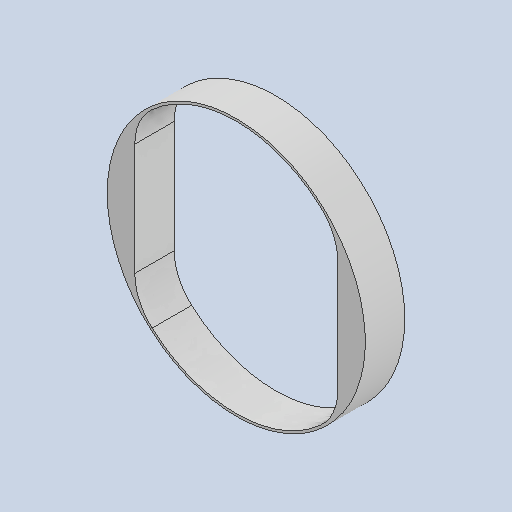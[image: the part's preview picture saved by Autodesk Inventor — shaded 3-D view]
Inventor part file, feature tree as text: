
AUTODESK INVENTOR PART (.ipt)
format: ipt  version: 2022 (Build 260153000, 153)  size: 126,976 bytes
history: native  units: in
note: dims shown in document units (in); Inventor stores cm internally (conversion verified against a paired STEP export)
features: other x3, sketch x1, plane x1, extrude x1, reference x1
ambient origin geometry x8: Origin, YZ Plane, XZ Plane, XY Plane, X Axis, Y Axis, Z Axis, Center Point
bodies: Solid1 (feature_tree)
feature tree (7):
  sketch  "Sketch1"  dims[d2=0.375in d3=0.0in d20=0.0157in d21=0.0394in]
  plane  "Work Plane1"
  extrude  "Extrusion1"  Depth=0.0157in
  reference  "Reference1"
  other  "<userpath>\Documents\CAD\guardSwerve1\Assembly1.iam"
  other  "Assembly1.iam"
  other  "Undercarriage:1"
